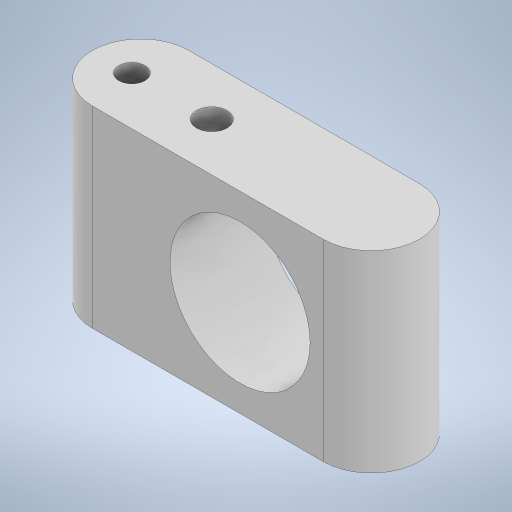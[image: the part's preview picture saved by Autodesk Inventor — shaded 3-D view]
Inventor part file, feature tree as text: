
AUTODESK INVENTOR PART (.ipt)
format: ipt  version: 2023 (Build 270158000, 158)  size: 301,568 bytes
history: native  units: in
note: dims shown in document units (in); Inventor stores cm internally (conversion verified against a paired STEP export)
features: extrude x4, sketch x3, fillet x1
ambient origin geometry x8: Origin, YZ Plane, XZ Plane, XY Plane, X Axis, Y Axis, Z Axis, Center Point
bodies: Solid1 (feature_tree)
feature tree (8):
  extrude  "Extrusion1"  Depth=0.3439in
  sketch  "Sketch2"  dims[d2=0.7033in d3=0.4331in]
  extrude  "Extrusion2"  Depth=0.4331in
  extrude  "Extrusion3"  Depth=0.4331in
  extrude  "Extrusion4"  Depth=0.4331in
  fillet  "Fillet1"  Radius=0.2756in
  sketch  "Sketch1"  dims[d0=0.6299in d1=0.3439in]
  sketch  "Sketch3"  dims[d4=0.4331in d5=0.4331in d6=0.4331in d7=0.2756in d8=0.1772in d9=0.4331in d10=0.0in d11=0.1772in d13=0.3594in d14=0.1181in d15=0.1378in d16=0.4331in d17=0.0in d18=0.1575in d19=0.0in d20=0.1575in d21=0.0in d22=0.2165in d23=1.4711in]
